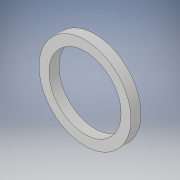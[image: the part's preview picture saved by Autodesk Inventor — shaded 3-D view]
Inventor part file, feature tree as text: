
AUTODESK INVENTOR PART (.ipt)
format: ipt  version: 2019 (Build 230136000, 136)  size: 103,936 bytes
history: native  units: mm
features: extrude x2, sketch x2
ambient origin geometry x8: Origin, YZ Plane, XZ Plane, XY Plane, X Axis, Y Axis, Z Axis, Center Point
bodies: Solid1 (feature_tree)
feature tree (4):
  extrude  "Extrusion1"  Depth=4.0mm TaperAngle=0.0deg
  extrude  "Extrusion2"  Depth=4.0mm TaperAngle=0.0deg
  sketch  "Sketch1"  dims[d0=37.0mm d1=4.0mm d2=0.0mm]
  sketch  "Sketch2"  dims[d3=29.0mm d4=4.0mm d5=0.0mm]
